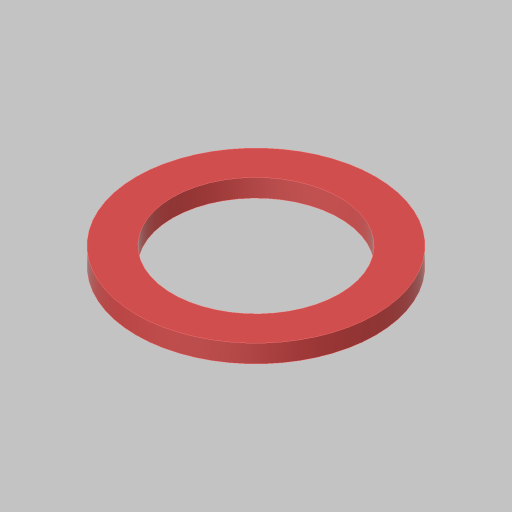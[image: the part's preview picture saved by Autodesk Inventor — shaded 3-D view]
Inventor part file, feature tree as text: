
AUTODESK INVENTOR PART (.ipt)
format: ipt  version: 2023.5 (Build 275446000, 446)  size: 98,816 bytes
history: native  units: in
note: dims shown in document units (in); Inventor stores cm internally (conversion verified against a paired STEP export)
features: extrude x1, sketch x1
ambient origin geometry x8: Origin, YZ Plane, XZ Plane, XY Plane, X Axis, Y Axis, Z Axis, Center Point
bodies: Solid1 (feature_tree)
feature tree (2):
  extrude  "Extrusion1"  Depth=0.0625in
  sketch  "Sketch1"  dims[d0=0.58in d1=0.125in d2=0.0625in d3=0.0in]
